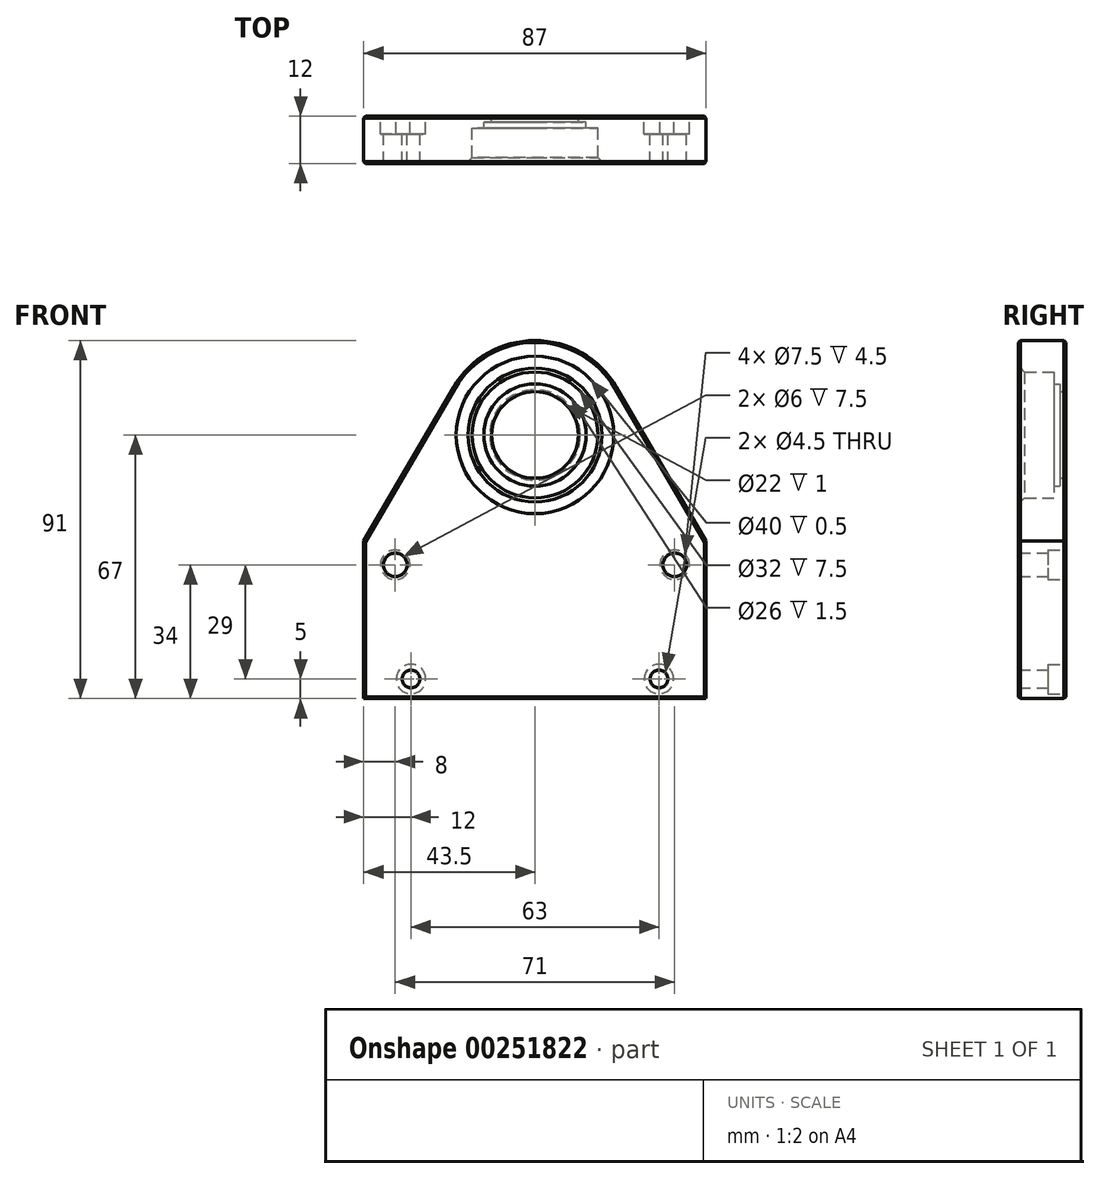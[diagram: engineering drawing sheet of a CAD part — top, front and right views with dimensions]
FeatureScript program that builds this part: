
annotation { "Feature Type Name" : "Feature", "Feature Type Description" : "" }
export const myFeature = defineFeature(function(context is Context, id is Id, definition is map)
    precondition{}
    {
        {
            var Q0;
            Q0=qCreatedBy(makeId("Front.planeOp"),FACE);
            var sketch = newSketch(context, id + "F0", { "sketchPlane" : qUnion([Q0])});
            skCircle(sketch, "E0", {"center": v(0, 0) * mm, "radius": 11 * mm});
            skLineSegment(sketch, "E1", {"start": v(-43.5, -27) * mm, "end": v(-43.5, -67) * mm});
            skLineSegment(sketch, "E2", {"start": v(-43.5, -67) * mm, "end": v(43.5, -67) * mm});
            skLineSegment(sketch, "E3", {"start": v(43.5, -67) * mm, "end": v(43.5, -27) * mm});
            skArc(sketch, "E4", {"start": v(20.74, 12.08) * mm, "mid": v(0, 24) * mm, "end": v(-20.74, 12.08) * mm});
            skLineSegment(sketch, "E5", {"start": v(-43.5, -27) * mm, "end": v(-20.74, 12.08) * mm});
            skLineSegment(sketch, "E6", {"start": v(43.5, -27) * mm, "end": v(20.74, 12.08) * mm});
            skLineSegment(sketch, "E7", {"start": v(-65.65, -33) * mm, "end": v(74.99, -33) * mm, "construction": true});
            skLineSegment(sketch, "E8", {"start": v(-60.57, -62) * mm, "end": v(80.5, -62) * mm, "construction": true});
            skPoint(sketch, "E9", {"position": v(-35.5, -33) * mm});
            skPoint(sketch, "E10", {"position": v(35.5, -33) * mm});
            skPoint(sketch, "E11", {"position": v(-31.5, -62) * mm});
            skPoint(sketch, "E12", {"position": v(31.5, -62) * mm});
            skSolve(sketch);
        }
        {
            var Q0;
            Q0=makeQuery(id+"F0.imprint","IMPRINT",FACE,{"disambiguationData":[TD([[makeQuery(id+"F0.imprint","IMPRINT",EDGE,{"derivedFrom":sQuery(id+"F0.wireOp",EDGE,"E0")}),-1.0]])]});
            extrude(context, id + "F1", {"entities" : qUnion([Q0]), "endBound" : BoundingType.SYMMETRIC, "depth" : 12 * mm});
        }
        {
            var Q0;
            Q0=makeQuery(id+"F1.opExtrude","CAP_FACE",FACE,{"disambiguationData":[OSD([sQuery(id+"F0.wireOp",EDGE,"E0"),sQuery(id+"F0.wireOp",EDGE,"E1"),sQuery(id+"F0.wireOp",EDGE,"E2"),sQuery(id+"F0.wireOp",EDGE,"E3"),sQuery(id+"F0.wireOp",EDGE,"E4"),sQuery(id+"F0.wireOp",EDGE,"E5"),sQuery(id+"F0.wireOp",EDGE,"E6")])],"isStart":true});
            var sketch = newSketch(context, id + "F2", { "sketchPlane" : qUnion([Q0])});
            skPoint(sketch, "E13.0", {"position": v(-35.5, -33) * mm});
            skPoint(sketch, "E14.0", {"position": v(35.5, -33) * mm});
            skPoint(sketch, "E15.0", {"position": v(-31.5, -62) * mm});
            skPoint(sketch, "E16.0", {"position": v(31.5, -62) * mm});
            skSolve(sketch);
        }
        {
            var Q0;
            Q0=sQuery(id+"F2.wireOp",VERTEX,"E13.0");
            var Q1;
            Q1=sQuery(id+"F2.wireOp",VERTEX,"E14.0");
            var Q2;
            Q2=makeQuery(id+"F1.opExtrude","SWEPT_BODY",BODY,{"disambiguationData":[OSD([sQuery(id+"F0.wireOp",EDGE,"E0"),sQuery(id+"F0.wireOp",EDGE,"E1"),sQuery(id+"F0.wireOp",EDGE,"E2"),sQuery(id+"F0.wireOp",EDGE,"E3"),sQuery(id+"F0.wireOp",EDGE,"E4"),sQuery(id+"F0.wireOp",EDGE,"E5"),sQuery(id+"F0.wireOp",EDGE,"E6")])]});
            hole(context, id + "F3", {"style" : HoleStyle.C_BORE, "endStyle" : HoleEndStyle.BLIND, "holeDiameter" : 6 * mm, "cBoreDiameter" : 7.5 * mm, "cBoreDepth" : 4.5 * mm, "holeDepth" : 18 * mm, "tappedDepth" : 12 * mm, "tapClearance" : 3, "locations" : qUnion([Q0, Q1]), "scope" : qUnion([Q2])});
        }
        {
            var Q0;
            Q0=sQuery(id+"F2.wireOp",VERTEX,"E15.0");
            var Q1;
            Q1=sQuery(id+"F2.wireOp",VERTEX,"E16.0");
            var Q2;
            Q2=makeQuery(id+"F1.opExtrude","SWEPT_BODY",BODY,{"disambiguationData":[OSD([sQuery(id+"F0.wireOp",EDGE,"E0"),sQuery(id+"F0.wireOp",EDGE,"E1"),sQuery(id+"F0.wireOp",EDGE,"E2"),sQuery(id+"F0.wireOp",EDGE,"E3"),sQuery(id+"F0.wireOp",EDGE,"E4"),sQuery(id+"F0.wireOp",EDGE,"E5"),sQuery(id+"F0.wireOp",EDGE,"E6")])]});
            hole(context, id + "F4", {"style" : HoleStyle.C_BORE, "endStyle" : HoleEndStyle.BLIND, "holeDiameter" : 4.5 * mm, "cBoreDiameter" : 7.5 * mm, "cBoreDepth" : 4.5 * mm, "holeDepth" : 18 * mm, "tappedDepth" : 12 * mm, "tapClearance" : 3, "locations" : qUnion([Q0, Q1]), "scope" : qUnion([Q2])});
        }
        {
            var Q0;
            Q0=qCreatedBy(makeId("Top.planeOp"),FACE);
            var sketch = newSketch(context, id + "F5", { "sketchPlane" : qUnion([Q0])});
            skLineSegment(sketch, "E17.0", {"start": v(11, 6) * mm, "end": v(0, 6) * mm});
            skLineSegment(sketch, "E18", {"start": v(0, 28.24) * mm, "end": v(0, -20.47) * mm});
            skLineSegment(sketch, "E19", {"start": v(0, -5.5) * mm, "end": v(20, -5.5) * mm});
            skLineSegment(sketch, "E20", {"start": v(20, -5.5) * mm, "end": v(20, -6) * mm});
            skLineSegment(sketch, "E21", {"start": v(0, -6) * mm, "end": v(20, -6) * mm});
            skLineSegment(sketch, "E22", {"start": v(0, -4.5) * mm, "end": v(16, -4.5) * mm});
            skLineSegment(sketch, "E23", {"start": v(16, -4.5) * mm, "end": v(17, -5.5) * mm});
            skLineSegment(sketch, "E24", {"start": v(16, 3) * mm, "end": v(16, -4.5) * mm});
            skLineSegment(sketch, "E25", {"start": v(13, 4.5) * mm, "end": v(13, 3) * mm});
            skLineSegment(sketch, "E26", {"start": v(11, 6) * mm, "end": v(11, 4.5) * mm});
            skLineSegment(sketch, "E27.trimOffspring", {"start": v(0, 4.5) * mm, "end": v(13, 4.5) * mm});
            skLineSegment(sketch, "E28.trimOffspring", {"start": v(0, 3) * mm, "end": v(16, 3) * mm});
            skPoint(sketch, "E29.start.orphan", {"position": v(-11, 6) * mm});
            skPoint(sketch, "E30.end.orphan", {"position": v(-16, -4.5) * mm});
            skSolve(sketch);
        }
        {
            var Q0;
            Q0 = qSketchRegion(id + "F5", true);
            var Q1;
            Q1=sQuery(id+"F5.wireOp",EDGE,"E18");
            revolve(context, id + "F6", {"operationType" : NewBodyOperationType.REMOVE, "entities" : qUnion([Q0]), "axis" : qUnion([Q1]), "revolveType" : RevolveType.FULL});
        }
        {
            var Q0;
            Q0=makeQuery(id+"F1.opExtrude","CAP_EDGE",EDGE,{"disambiguationData":[OSD([sQuery(id+"F0.wireOp",EDGE,"E0")])],"isStart":true});
            var Q1;
            Q1=makeQuery(id+"F1.opExtrude","CAP_EDGE",EDGE,{"disambiguationData":[OSD([sQuery(id+"F0.wireOp",EDGE,"E6")])],"isStart":true});
            var Q2;
            Q2=makeQuery(id+"F1.opExtrude","CAP_EDGE",EDGE,{"disambiguationData":[OSD([sQuery(id+"F0.wireOp",EDGE,"E4")])],"isStart":true});
            var Q3;
            Q3=makeQuery(id+"F1.opExtrude","CAP_EDGE",EDGE,{"disambiguationData":[OSD([sQuery(id+"F0.wireOp",EDGE,"E3")])],"isStart":true});
            var Q4;
            Q4=makeQuery(id+"F1.opExtrude","CAP_EDGE",EDGE,{"disambiguationData":[OSD([sQuery(id+"F0.wireOp",EDGE,"E2")])],"isStart":true});
            var Q5;
            Q5=makeQuery(id+"F1.opExtrude","CAP_EDGE",EDGE,{"disambiguationData":[OSD([sQuery(id+"F0.wireOp",EDGE,"E1")])],"isStart":true});
            var Q6;
            Q6=makeQuery(id+"F1.opExtrude","CAP_EDGE",EDGE,{"disambiguationData":[OSD([sQuery(id+"F0.wireOp",EDGE,"E5")])],"isStart":true});
            var Q7;
            Q7=makeQuery(id+"F1.opExtrude","CAP_EDGE",EDGE,{"disambiguationData":[OSD([sQuery(id+"F0.wireOp",EDGE,"E4")])],"isStart":false});
            var Q8;
            Q8=makeQuery(id+"F1.opExtrude","CAP_EDGE",EDGE,{"disambiguationData":[OSD([sQuery(id+"F0.wireOp",EDGE,"E6")])],"isStart":false});
            var Q9;
            Q9=makeQuery(id+"F1.opExtrude","CAP_EDGE",EDGE,{"disambiguationData":[OSD([sQuery(id+"F0.wireOp",EDGE,"E5")])],"isStart":false});
            var Q10;
            Q10=makeQuery(id+"F1.opExtrude","CAP_EDGE",EDGE,{"disambiguationData":[OSD([sQuery(id+"F0.wireOp",EDGE,"E1")])],"isStart":false});
            var Q11;
            Q11=makeQuery(id+"F1.opExtrude","CAP_EDGE",EDGE,{"disambiguationData":[OSD([sQuery(id+"F0.wireOp",EDGE,"E3")])],"isStart":false});
            var Q12;
            Q12=makeQuery(id+"F1.opExtrude","CAP_EDGE",EDGE,{"disambiguationData":[OSD([sQuery(id+"F0.wireOp",EDGE,"E2")])],"isStart":false});
            chamfer(context, id + "F7", {"entities" : qUnion([Q0, Q1, Q2, Q3, Q4, Q5, Q6, Q7, Q8, Q9, Q10, Q11, Q12]), "width" : .5 * mm, "tangentPropagation" : true});
        }
    });
